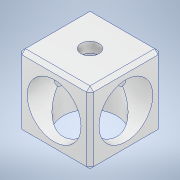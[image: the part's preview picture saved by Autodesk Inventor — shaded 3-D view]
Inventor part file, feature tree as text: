
AUTODESK INVENTOR PART (.ipt)
format: ipt  version: 2022 (Build 260153000, 153)  size: 157,184 bytes
history: imported  units: in
note: dims shown in document units (in); Inventor stores cm internally (conversion verified against a paired STEP export)
features: imported_body x1
ambient origin geometry x8: Origin, YZ Plane, XZ Plane, XY Plane, X Axis, Y Axis, Z Axis, Center Point
bodies: Solid1 (imported_parasolid), Body1 (imported_parasolid)
feature tree (1):
  imported_body  NMx_Import_Brep_tag  [imported B-rep: ~7 faces, bbox_mm=[0.0, 0.0, 0.0]]
